# Revit family: JOMA_Balksko kombi_Grundform 260
name_source: partatom
category: Structural Connections
revit_build: Autodesk Revit Structure 2012 (Build: 20110309_2315(x64)
units: mm (PartAtom-declared; Revit-internal decimal feet)

## types (4) — shared parameters
D = 37 mm  [stored 0.121391 ft]
Default Elevation = 1219 mm
E = 37 mm  [stored 0.121391 ft]
F = 70 mm  [stored 0.229659 ft]
Grundform 260 = Yes
Länk Joma Dimensioneringsverktyg = http://www.joma.se
Material = Varmförzinkad stålplåt
Typ = GRUNDFORM 260
Vikt = 0,26
X = 35 mm
Y = 63 mm  [stored 0.206693 ft]

## per-type parameters (varying)
| type | A | B |
| 5240110  40x110 | 40 mm  [stored 0.131234 ft] | 110 mm  [stored 0.360892 ft] |
| 5245108  45x108 | 45 mm  [stored 0.147638 ft] | 108 mm  [stored 0.354331 ft] |
| 5251105  51x105 | 51 mm | 105 mm  [stored 0.344488 ft] |
| 5260100  60x100 | 60 mm  [stored 0.19685 ft] | 100 mm  [stored 0.328084 ft] |

note: [stored X ft] marks values corroborated as IEEE doubles in the binary element streams (Revit-internal decimal feet)

## geometry (parser evidence)
native form markers: Sweep x2
no freeform markers — native parametric forms only
